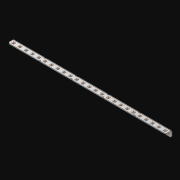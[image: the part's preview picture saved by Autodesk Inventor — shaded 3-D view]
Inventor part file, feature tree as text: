
AUTODESK INVENTOR PART (.ipt)
format: ipt  version: 2021 (Build 250183000, 183)  size: 775,168 bytes
history: native  units: in
note: dims shown in document units (in); Inventor stores cm internally (conversion verified against a paired STEP export)
features: extrude x51, other x50, sketch x3, pattern_linear x1, sheet_metal_op x1
ambient origin geometry x8: Origin, YZ Plane, XZ Plane, XY Plane, X Axis, Y Axis, Z Axis, Center Point
bodies: Solid1 (feature_tree)
feature tree (106):
  pattern_linear  "Rectangular Pattern1"  Spacing1=0.063in  [1 undecoded]
  extrude  "Extrusion1"  Depth=0.5in
  sketch  "Sketch1"  dims[d0=0.182in]
  other  "Srf1"
  sketch  "Sketch2"  dims[d1=0.063in d2=0.0in]
  other  "Srf2"
  other  "Srf3"
  other  "Srf5"
  other  "Srf7"
  other  "Srf9"
  other  "Srf11"
  other  "Srf13"
  other  "Srf15"
  other  "Srf17"
  other  "Srf19"
  other  "Srf21"
  other  "Srf23"
  other  "Srf25"
  other  "Srf27"
  other  "Srf29"
  other  "Srf31"
  other  "Srf33"
  other  "Srf35"
  other  "Srf37"
  other  "Srf39"
  other  "Srf41"
  other  "Srf43"
  other  "Srf45"
  other  "Srf47"
  other  "Srf49"
  other  "Srf4"
  other  "Srf6"
  other  "Srf8"
  other  "Srf10"
  other  "Srf12"
  other  "Srf14"
  other  "Srf16"
  other  "Srf18"
  other  "Srf20"
  other  "Srf22"
  other  "Srf24"
  other  "Srf26"
  other  "Srf28"
  other  "Srf30"
  other  "Srf32"
  other  "Srf34"
  other  "Srf36"
  other  "Srf38"
  other  "Srf40"
  other  "Srf42"
  other  "Srf44"
  other  "Srf46"
  other  "Srf48"
  other  "Srf50"
  sketch  "Sketch3"  dims[d3=0.182in d4=0.063in d5=0.0in d8=0.5in d9=5.0in d10=0.0in]
  sheet_metal_op  "Fold1"
  extrude  "ExtrusionSrf1"  Depth=5.0in TaperAngle=0.0deg
  extrude  "ExtrusionSrf2"  [1 undecoded]
  extrude  "ExtrusionSrf3"  [1 undecoded]
  extrude  "ExtrusionSrf4"  [1 undecoded]
  extrude  "ExtrusionSrf5"  [1 undecoded]
  extrude  "ExtrusionSrf6"  [1 undecoded]
  extrude  "ExtrusionSrf7"  [1 undecoded]
  extrude  "ExtrusionSrf8"  [1 undecoded]
  extrude  "ExtrusionSrf9"  [1 undecoded]
  extrude  "ExtrusionSrf10"  [1 undecoded]
  extrude  "ExtrusionSrf11"  [1 undecoded]
  extrude  "ExtrusionSrf12"  [1 undecoded]
  extrude  "ExtrusionSrf13"  [1 undecoded]
  extrude  "ExtrusionSrf14"  [1 undecoded]
  extrude  "ExtrusionSrf15"  [1 undecoded]
  extrude  "ExtrusionSrf16"  [1 undecoded]
  extrude  "ExtrusionSrf17"  [1 undecoded]
  extrude  "ExtrusionSrf18"  [1 undecoded]
  extrude  "ExtrusionSrf19"  [1 undecoded]
  extrude  "ExtrusionSrf20"  [1 undecoded]
  extrude  "ExtrusionSrf21"  [1 undecoded]
  extrude  "ExtrusionSrf22"  [1 undecoded]
  extrude  "ExtrusionSrf23"  [1 undecoded]
  extrude  "ExtrusionSrf24"  [1 undecoded]
  extrude  "ExtrusionSrf25"  [1 undecoded]
  extrude  "ExtrusionSrf26"  [1 undecoded]
  extrude  "ExtrusionSrf37"  [1 undecoded]
  extrude  "ExtrusionSrf38"  [1 undecoded]
  extrude  "ExtrusionSrf39"  [1 undecoded]
  extrude  "ExtrusionSrf40"  [1 undecoded]
  extrude  "ExtrusionSrf41"  [1 undecoded]
  extrude  "ExtrusionSrf42"  [1 undecoded]
  extrude  "ExtrusionSrf43"  [1 undecoded]
  extrude  "ExtrusionSrf44"  [1 undecoded]
  extrude  "ExtrusionSrf45"  [1 undecoded]
  extrude  "ExtrusionSrf46"  [1 undecoded]
  extrude  "ExtrusionSrf47"  [1 undecoded]
  extrude  "ExtrusionSrf48"  [1 undecoded]
  extrude  "ExtrusionSrf49"  [1 undecoded]
  extrude  "ExtrusionSrf50"  [1 undecoded]
  extrude  "ExtrusionSrf51"  [1 undecoded]
  extrude  "ExtrusionSrf52"  [1 undecoded]
  extrude  "ExtrusionSrf53"  [1 undecoded]
  extrude  "ExtrusionSrf54"  [1 undecoded]
  extrude  "ExtrusionSrf55"  [1 undecoded]
  extrude  "ExtrusionSrf56"  [1 undecoded]
  extrude  "ExtrusionSrf57"  [1 undecoded]
  extrude  "ExtrusionSrf58"  [1 undecoded]
  extrude  "ExtrusionSrf59"  [1 undecoded]
  extrude  "ExtrusionSrf60"  [1 undecoded]
note: 50 required parameter values undecoded (feature->parameter linkage not recoverable at this tier; creation-order binding heuristic only, values carry confidence <= 0.55)
